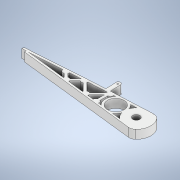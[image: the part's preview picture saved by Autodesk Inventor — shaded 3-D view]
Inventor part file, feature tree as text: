
AUTODESK INVENTOR PART (.ipt)
format: ipt  version: 2022 (Build 260153000, 153)  size: 390,656 bytes
history: native  units: mm
features: extrude x1, sketch x1
ambient origin geometry x8: Origin, YZ Plane, XZ Plane, XY Plane, X Axis, Y Axis, Z Axis, Center Point
bodies: Body1 (feature_tree)
feature tree (2):
  extrude  "Extrusion6"  Depth=10.0mm
  sketch  "Sketch1"  dims[d31=34.456mm d50=368.759386mm d57=16.0mm d69=8.0mm d70=23.0mm d71=8.0mm d73=16.0mm d80=19.0mm d81=16.0mm d82=1.0mm d83=1.0mm d84=1.0mm d85=1.0mm d86=1.0mm d87=0.8mm d88=1.0mm d90=19.0mm d94=5.0mm d95=5.0mm d105=5.0mm d106=5.0mm d108=2.0mm d109=19.0mm d114=5.0mm d115=5.0mm d116=24.0mm d117=2.5mm d118=2.5mm d123=2.5mm d124=2.5mm d125=10.0mm d126=24.0mm d127=24.0mm d128=27.0mm d135=0.5mm d136=45.0deg d139=7.0mm d165=45.0deg d169=27.0mm d175=90.0deg d181=45.0deg d185=7.0mm d186=45.0deg d190=7.0mm d191=45.0deg d197=90.0deg d203=90.0deg d206=7.0mm d209=40.0mm d210=10.0mm d211=0.0mm d212=41.0mm d213=20.0mm d214=23.0mm d215=5.0mm d216=15.0mm d217=2.0mm d218=12.0mm d219=1.5mm]
